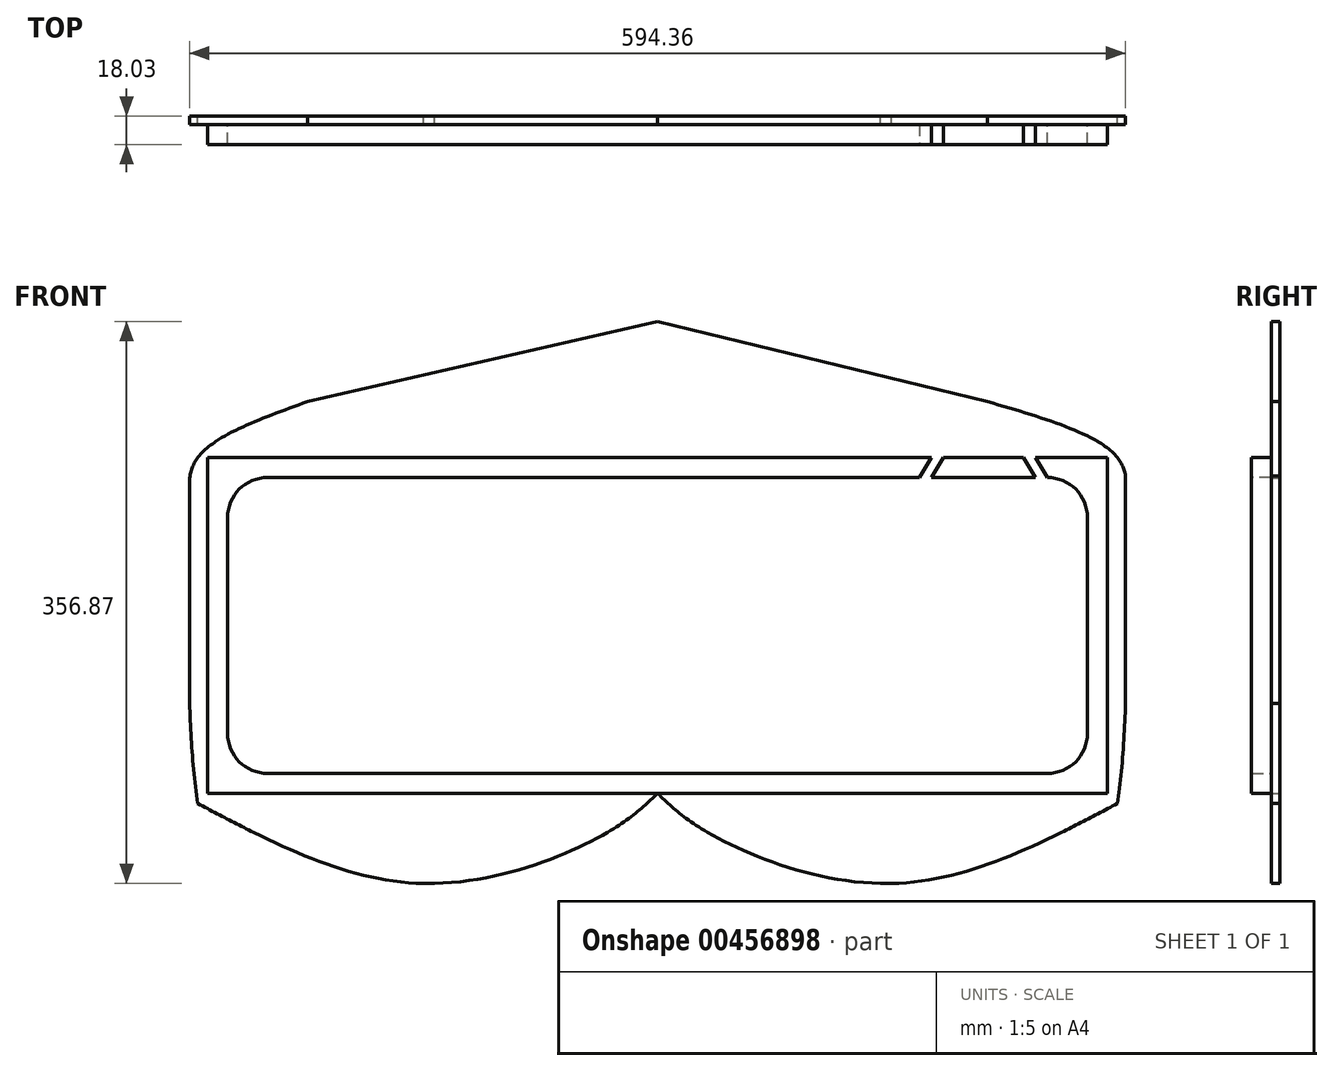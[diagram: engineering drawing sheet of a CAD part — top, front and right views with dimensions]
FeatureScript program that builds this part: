
annotation { "Feature Type Name" : "Feature", "Feature Type Description" : "" }
export const myFeature = defineFeature(function(context is Context, id is Id, definition is map)
    precondition{}
    {
        {
            var Q0;
            Q0=qCreatedBy(makeId("Front.planeOp"),FACE);
            var sketch = newSketch(context, id + "F0", { "sketchPlane" : qUnion([Q0])});
            skLineSegment(sketch, "E0.bottom", {"start": v(0, 0) * mm, "end": v(-584.2, 0) * mm});
            skLineSegment(sketch, "E0.top", {"start": v(0, 219.7) * mm, "end": v(-584.2, 219.7) * mm});
            skLineSegment(sketch, "E0.left", {"start": v(0, 0) * mm, "end": v(0, 219.7) * mm});
            skLineSegment(sketch, "E0.right", {"start": v(-584.2, 0) * mm, "end": v(-584.2, 219.7) * mm});
            skPoint(sketch, "E1", {"position": v(-292.1, 219.7) * mm});
            skSolve(sketch);
        }
        {
            var Q0;
            Q0=makeQuery(id+"F0.imprint","IMPRINT",FACE,{"disambiguationData":[TD([[makeQuery(id+"F0.imprint","IMPRINT",EDGE,{"derivedFrom":sQuery(id+"F0.wireOp",EDGE,"E0.bottom")}),-1.0]])]});
            extrude(context, id + "F1", {"entities" : qUnion([Q0]), "depth" : 5.33 * mm});
        }
        {
            var Q0;
            Q0=makeQuery(id+"F1.opExtrude","CAP_FACE",FACE,{"disambiguationData":[OSD([sQuery(id+"F0.wireOp",EDGE,"E0.bottom"),sQuery(id+"F0.wireOp",EDGE,"E0.top"),sQuery(id+"F0.wireOp",EDGE,"E0.left"),sQuery(id+"F0.wireOp",EDGE,"E0.right")])],"isStart":false});
            var sketch = newSketch(context, id + "F2", { "sketchPlane" : qUnion([Q0])});
            skLineSegment(sketch, "E2", {"start": v(-577.85, 219.7) * mm, "end": v(-577.85, 6.35) * mm});
            skLineSegment(sketch, "E3", {"start": v(-577.85, 6.35) * mm, "end": v(-6.35, 6.35) * mm});
            skLineSegment(sketch, "E4", {"start": v(-6.35, 6.35) * mm, "end": v(-6.35, 219.71) * mm});
            skLineSegment(sketch, "E5", {"start": v(-6.35, 219.71) * mm, "end": v(-577.85, 219.7) * mm});
            skLineSegment(sketch, "E6", {"start": v(-565.15, 207) * mm, "end": v(-565.15, 19.05) * mm});
            skLineSegment(sketch, "E7", {"start": v(-565.15, 19.05) * mm, "end": v(-19.05, 19.05) * mm});
            skLineSegment(sketch, "E8", {"start": v(-19.05, 19.05) * mm, "end": v(-19.05, 207.01) * mm});
            skLineSegment(sketch, "E9", {"start": v(-19.05, 207.01) * mm, "end": v(-565.15, 207) * mm});
            skSolve(sketch);
        }
        {
            var Q0;
            Q0=makeQuery(id+"F2.imprint","IMPRINT",FACE,{"disambiguationData":[TD([[makeQuery(id+"F2.imprint","IMPRINT",EDGE,{"derivedFrom":sQuery(id+"F2.wireOp",EDGE,"E2")}),1.0]])]});
            extrude(context, id + "F3", {"entities" : qUnion([Q0]), "operationType" : NewBodyOperationType.ADD, "depth" : 12.7 * mm});
        }
        {
            var Q0;
            Q0=makeQuery(id+"F3.opExtrude","SWEPT_EDGE",EDGE,{"disambiguationData":[OSD([sQuery(id+"F2.wireOp",EDGE,"E6"),sQuery(id+"F2.wireOp",EDGE,"E9")])]});
            var Q1;
            Q1=makeQuery(id+"F3.opExtrude","SWEPT_EDGE",EDGE,{"disambiguationData":[OSD([sQuery(id+"F2.wireOp",EDGE,"E8"),sQuery(id+"F2.wireOp",EDGE,"E9")])]});
            var Q2;
            Q2=makeQuery(id+"F3.opExtrude","SWEPT_EDGE",EDGE,{"disambiguationData":[OSD([sQuery(id+"F2.wireOp",EDGE,"E7"),sQuery(id+"F2.wireOp",EDGE,"E8")])]});
            var Q3;
            Q3=makeQuery(id+"F3.opExtrude","SWEPT_EDGE",EDGE,{"disambiguationData":[OSD([sQuery(id+"F2.wireOp",EDGE,"E6"),sQuery(id+"F2.wireOp",EDGE,"E7")])]});
            fillet(context, id + "F4", {"entities" : qUnion([Q0, Q1, Q2, Q3]), "radius" : 25.4 * mm, "tangentPropagation" : true, "allowEdgeOverflow" : false});
        }
        {
            var Q0;
            Q0=makeQuery(id+"F3.opExtrude","CAP_FACE",FACE,{"disambiguationData":[OSD([sQuery(id+"F2.wireOp",EDGE,"E2"),sQuery(id+"F2.wireOp",EDGE,"E3"),sQuery(id+"F2.wireOp",EDGE,"E4"),sQuery(id+"F2.wireOp",EDGE,"E5"),sQuery(id+"F2.wireOp",EDGE,"E6"),sQuery(id+"F2.wireOp",EDGE,"E7"),sQuery(id+"F2.wireOp",EDGE,"E8"),sQuery(id+"F2.wireOp",EDGE,"E9")])],"isStart":false});
            var sketch = newSketch(context, id + "F5", { "sketchPlane" : qUnion([Q0])});
            skPoint(sketch, "E10", {"position": v(-118.11, 219.7) * mm});
            skPoint(sketch, "E11", {"position": v(-110.5, 219.7) * mm});
            skPoint(sketch, "E12", {"position": v(-59.69, 219.7) * mm});
            skPoint(sketch, "E13", {"position": v(-52.07, 219.7) * mm});
            skPoint(sketch, "E14", {"position": v(-376.28, 272.75) * mm});
            skPoint(sketch, "E15", {"position": v(-12.7, 0) * mm});
            skPoint(sketch, "E16", {"position": v(-20.32, 0) * mm});
            skLineSegment(sketch, "E17", {"start": v(-20.32, 0) * mm, "end": v(-12.7, 0) * mm});
            skPoint(sketch, "E18", {"position": v(-118.11, 207.01) * mm});
            skPoint(sketch, "E19", {"position": v(-125.73, 207.01) * mm});
            skLineSegment(sketch, "E20", {"start": v(-125.73, 207.01) * mm, "end": v(-118.11, 219.7) * mm});
            skLineSegment(sketch, "E21", {"start": v(-125.73, 207.01) * mm, "end": v(-118.11, 207.01) * mm});
            skLineSegment(sketch, "E22", {"start": v(-118.11, 207.01) * mm, "end": v(-110.5, 219.7) * mm});
            skLineSegment(sketch, "E23", {"start": v(-118.11, 219.7) * mm, "end": v(-110.5, 219.7) * mm});
            skLineSegment(sketch, "E24", {"start": v(-59.69, 219.7) * mm, "end": v(-52.07, 219.7) * mm});
            skLineSegment(sketch, "E25", {"start": v(-110.5, 219.7) * mm, "end": v(-59.69, 219.7) * mm});
            skLineSegment(sketch, "E26", {"start": v(-59.69, 219.7) * mm, "end": v(-110.5, 219.7) * mm});
            skLineSegment(sketch, "E27", {"start": v(-110.5, 219.7) * mm, "end": v(-113.58, 214.56) * mm});
            skPoint(sketch, "E28", {"position": v(-44.45, 207.01) * mm});
            skPoint(sketch, "E29", {"position": v(-52.07, 207.01) * mm});
            skLineSegment(sketch, "E30", {"start": v(-59.69, 219.7) * mm, "end": v(-52.07, 207.01) * mm});
            skLineSegment(sketch, "E31", {"start": v(-52.07, 219.7) * mm, "end": v(-44.45, 207.01) * mm});
            skLineSegment(sketch, "E32", {"start": v(-52.07, 207.01) * mm, "end": v(-44.45, 207.01) * mm});
            skLineSegment(sketch, "E33", {"start": v(-52.07, 219.7) * mm, "end": v(-59.69, 219.7) * mm});
            skPoint(sketch, "E34", {"position": v(-56.6, 214.56) * mm});
            skLineSegment(sketch, "E35", {"start": v(-113.58, 214.56) * mm, "end": v(-56.6, 214.56) * mm});
            skSolve(sketch);
        }
        {
            var Q0;
            Q0=makeQuery(id+"F5.imprint","IMPRINT",FACE,{"disambiguationData":[TD([[makeQuery(id+"F5.imprint","IMPRINT",EDGE,{"derivedFrom":sQuery(id+"F5.wireOp",EDGE,"E20")}),-1.0]])]});
            var Q1;
            {var subQ8=sQuery(id+"F5.wireOp",EDGE,"RZINdJYM-ykuw-GilU-JIjt-DnibDYUsXZuo");Q1=makeQuery(id+"F5.imprint","IMPRINT",FACE,{"disambiguationData":[TD([[makeQuery(id+"F5.imprint","IMPRINT",EDGE,{"derivedFrom":subQ8}),1.0]])]});}
            var Q2;
            Q2=makeQuery(id+"F5.imprint","IMPRINT",FACE,{"disambiguationData":[TD([[makeQuery(id+"F5.imprint","IMPRINT",EDGE,{"derivedFrom":sQuery(id+"F5.wireOp",EDGE,"RZINdJYM-ykuw-GilU-JIjt-DnibDYUsXZuo")}),-1.0]])]});
            var Q3;
            Q3=makeQuery(id+"F5.imprint","IMPRINT",FACE,{"disambiguationData":[TD([[makeQuery(id+"F5.imprint","IMPRINT",EDGE,{"derivedFrom":sQuery(id+"F5.wireOp",EDGE,"NQJIxGkc-Vixr-o2zM-VUe3-bVQ5EoZFKsab")}),1.0]])]});
            var Q4;
            Q4=makeQuery(id+"F5.imprint","IMPRINT",FACE,{"disambiguationData":[TD([[makeQuery(id+"F5.imprint","IMPRINT",EDGE,{"derivedFrom":sQuery(id+"F5.wireOp",EDGE,"E30")}),1.0]])]});
            var Q5;
            {var subQ0=sQuery(id+"F5.wireOp",EDGE,"E26");Q5=makeQuery(id+"F5.imprint","IMPRINT",FACE,{"disambiguationData":[TD([[makeQuery(id+"F5.imprint","IMPRINT",EDGE,{"derivedFrom":subQ0}),1.0]])]});}
            extrude(context, id + "F6", {"entities" : qUnion([Q0, Q1, Q2, Q3, Q4, Q5]), "operationType" : NewBodyOperationType.REMOVE, "oppositeDirection" : true, "depth" : 12.7 * mm});
        }
        {
            var Q0;
            Q0=makeQuery(id+"F1.opExtrude","CAP_FACE",FACE,{"disambiguationData":[OSD([sQuery(id+"F0.wireOp",EDGE,"E0.bottom"),sQuery(id+"F0.wireOp",EDGE,"E0.top"),sQuery(id+"F0.wireOp",EDGE,"E0.left"),sQuery(id+"F0.wireOp",EDGE,"E0.right")])],"isStart":true});
            var sketch = newSketch(context, id + "F7", { "sketchPlane" : qUnion([Q0])});
            skLineSegment(sketch, "E36", {"start": v(0, 0) * mm, "end": v(-5.08, 0) * mm});
            skLineSegment(sketch, "E37", {"start": v(-5.08, 0) * mm, "end": v(-5.08, 229.87) * mm});
            skLineSegment(sketch, "E38", {"start": v(-5.08, 229.87) * mm, "end": v(589.28, 229.87) * mm});
            skLineSegment(sketch, "E39", {"start": v(589.28, 229.87) * mm, "end": v(589.28, 0) * mm});
            skLineSegment(sketch, "E40", {"start": v(589.28, 0) * mm, "end": v(584.2, 0) * mm});
            skPoint(sketch, "E41", {"position": v(589.28, 114.93) * mm});
            skPoint(sketch, "E42", {"position": v(584.2, 109.85) * mm});
            skPoint(sketch, "E43", {"position": v(292.1, 229.87) * mm});
            skPoint(sketch, "E44", {"position": v(292.1, 219.7) * mm});
            skPoint(sketch, "E45", {"position": v(-5.08, 114.93) * mm});
            skPoint(sketch, "E46", {"position": v(0, 109.85) * mm});
            skPoint(sketch, "E47", {"position": v(538.48, 229.87) * mm});
            skPoint(sketch, "E48", {"position": v(45.72, 229.87) * mm});
            skPoint(sketch, "E49", {"position": v(-5.08, 191.77) * mm});
            skPoint(sketch, "E50", {"position": v(589.28, 191.77) * mm});
            skPoint(sketch, "E51", {"position": v(584.2, 183.25) * mm});
            skPoint(sketch, "E52", {"position": v(0, 176.13) * mm});
            skPoint(sketch, "E53", {"position": v(589.28, 63.5) * mm});
            skPoint(sketch, "E54", {"position": v(-5.08, 63.5) * mm});
            skPoint(sketch, "E55", {"position": v(0, 219.7) * mm});
            skPoint(sketch, "E56", {"position": v(584.2, 219.7) * mm});
            skPoint(sketch, "E57", {"position": v(393.7, 219.7) * mm});
            skPoint(sketch, "E58", {"position": v(190.5, 219.7) * mm});
            skLineSegment(sketch, "E59", {"start": v(292.1, 219.7) * mm, "end": v(-5.08, 229.87) * mm});
            skLineSegment(sketch, "E60", {"start": v(292.1, 219.7) * mm, "end": v(589.28, 229.87) * mm});
            skLineSegment(sketch, "E61", {"start": v(589.28, -18.42) * mm, "end": v(-5.08, -18.42) * mm});
            skLineSegment(sketch, "E62", {"start": v(589.28, 0) * mm, "end": v(589.28, -18.42) * mm});
            skLineSegment(sketch, "E63", {"start": v(292.1, 229.87) * mm, "end": v(292.1, 306.07) * mm});
            skPoint(sketch, "E64", {"position": v(292.1, -18.42) * mm});
            skLineSegment(sketch, "E65", {"start": v(589.28, -18.42) * mm, "end": v(589.28, -50.8) * mm});
            skLineSegment(sketch, "E66", {"start": v(589.28, -50.8) * mm, "end": v(292.1, -50.8) * mm});
            skPoint(sketch, "E67", {"position": v(292.1, 0) * mm});
            skPoint(sketch, "E68", {"position": v(440.69, -50.8) * mm});
            skLineSegment(sketch, "E69", {"start": v(292.1, -50.8) * mm, "end": v(-4.91, -50.8) * mm});
            skLineSegment(sketch, "E70", {"start": v(-4.91, -50.8) * mm, "end": v(-5.08, -18.42) * mm});
            skPoint(sketch, "E71", {"position": v(143.6, -50.8) * mm});
            skPoint(sketch, "E72", {"position": v(551.18, -18.42) * mm});
            skPoint(sketch, "E73", {"position": v(33.02, -18.42) * mm});
            skPoint(sketch, "E74", {"position": v(6.35, 219.7) * mm});
            skPoint(sketch, "E75", {"position": v(577.85, 219.7) * mm});
            skPoint(sketch, "E76", {"position": v(6.35, 0) * mm});
            skPoint(sketch, "E77", {"position": v(577.85, 0) * mm});
            skPoint(sketch, "E78", {"position": v(82.55, 229.87) * mm});
            skPoint(sketch, "E79", {"position": v(514.35, 229.87) * mm});
            skLineSegment(sketch, "E80", {"start": v(82.55, 229.87) * mm, "end": v(82.55, 255.27) * mm});
            skLineSegment(sketch, "E81", {"start": v(514.35, 229.87) * mm, "end": v(514.35, 255.27) * mm});
            skLineSegment(sketch, "E82", {"start": v(292.1, 0) * mm, "end": v(292.1, 6.35) * mm});
            skPoint(sketch, "E83", {"position": v(323.85, -18.42) * mm});
            skPoint(sketch, "E84", {"position": v(260.35, -18.42) * mm});
            skFitSpline(sketch, "E85", {"points": [v(292.1, 6.35) * mm, v(323.85, -18.42) * mm, v(440.69, -50.8) * mm, v(584.2, 0) * mm], "startDerivative": vector(117.09, -111.78) * mm, "endDerivative": vector(338.96, 179.53) * mm});
            skFitSpline(sketch, "E86", {"points": [v(292.1, 6.35) * mm, v(260.35, -18.42) * mm, v(143.6, -50.8) * mm, v(0, 0) * mm], "startDerivative": vector(-117.11, -111.77) * mm, "endDerivative": vector(-339.14, 179.5) * mm});
            skFitSpline(sketch, "E87", {"points": [v(514.35, 255.27) * mm, v(292.1, 306.07) * mm], "startDerivative": vector(-222.25, 50.8) * mm, "endDerivative": vector(-222.25, 50.8) * mm});
            skFitSpline(sketch, "E88", {"points": [v(514.35, 255.27) * mm, v(584.2, 219.7) * mm, v(589.28, 191.77) * mm], "startDerivative": vector(142.6, -51.54) * mm, "endDerivative": vector(-4.96, -77.63) * mm});
            skFitSpline(sketch, "E89", {"points": [v(584.2, 0) * mm, v(589.28, 63.5) * mm, v(589.28, 114.93) * mm], "startDerivative": vector(16.08, 110.78) * mm, "endDerivative": vector(0, 114.64) * mm});
            skFitSpline(sketch, "E90", {"points": [v(0, 0) * mm, v(-5.08, 63.5) * mm, v(-5.08, 114.94) * mm], "startDerivative": vector(-15.41, 98.4) * mm, "endDerivative": vector(0, 110.04) * mm});
            skFitSpline(sketch, "E91", {"points": [v(292.1, 306.07) * mm, v(82.55, 255.27) * mm], "startDerivative": vector(-209.55, -50.8) * mm, "endDerivative": vector(-209.55, -50.8) * mm});
            skFitSpline(sketch, "E92", {"points": [v(82.55, 255.27) * mm, v(0, 219.7) * mm, v(-5.08, 191.77) * mm], "startDerivative": vector(-165.7, -48.47) * mm, "endDerivative": vector(6.54, -81.62) * mm});
            skSolve(sketch);
        }
        {
            var Q0;
            {var subQ0=sQuery(id+"F7.wireOp",EDGE,"E82");Q0=makeQuery(id+"F7.imprint","IMPRINT",FACE,{"disambiguationData":[TD([[makeQuery(id+"F7.imprint","IMPRINT",EDGE,{"derivedFrom":subQ0}),1.0]])]});}
            var Q1;
            {var subQ0=sQuery(id+"F7.wireOp",EDGE,"E82");Q1=makeQuery(id+"F7.imprint","IMPRINT",FACE,{"disambiguationData":[TD([[makeQuery(id+"F7.imprint","IMPRINT",EDGE,{"derivedFrom":subQ0}),-1.0]])]});}
            extrude(context, id + "F8", {"entities" : qUnion([Q0, Q1]), "operationType" : NewBodyOperationType.REMOVE, "depth" : -5.33 * mm});
        }
        {
            var Q0;
            {var subQ0=sQuery(id+"F7.wireOp",EDGE,"E80");Q0=makeQuery(id+"F7.imprint","IMPRINT",FACE,{"disambiguationData":[TD([[makeQuery(id+"F7.imprint","IMPRINT",EDGE,{"derivedFrom":subQ0}),1.0]])]});}
            var Q1;
            {var subQ0=sQuery(id+"F7.wireOp",EDGE,"E63");Q1=makeQuery(id+"F7.imprint","IMPRINT",FACE,{"disambiguationData":[TD([[makeQuery(id+"F7.imprint","IMPRINT",EDGE,{"derivedFrom":subQ0}),1.0]])]});}
            var Q2;
            {var subQ0=sQuery(id+"F7.wireOp",EDGE,"E63");Q2=makeQuery(id+"F7.imprint","IMPRINT",FACE,{"disambiguationData":[TD([[makeQuery(id+"F7.imprint","IMPRINT",EDGE,{"derivedFrom":subQ0}),-1.0]])]});}
            var Q3;
            {var subQ0=sQuery(id+"F7.wireOp",EDGE,"E81");Q3=makeQuery(id+"F7.imprint","IMPRINT",FACE,{"disambiguationData":[TD([[makeQuery(id+"F7.imprint","IMPRINT",EDGE,{"derivedFrom":subQ0}),-1.0]])]});}
            var Q4;
            {var subQ0=sQuery(id+"F7.wireOp",EDGE,"E60");var subQ3=sQuery(id+"F7.wireOp",EDGE,"c924a81b-7c33-454b-bec7-e8dcdf9a45a6");var subQ4=makeQuery(id+"F7.imprint","INTERSECT",VERTEX,{"derivedFrom":[subQ0,subQ3]});Q4=makeQuery(id+"F7.imprint","IMPRINT",FACE,{"disambiguationData":[TD([[makeQuery(id+"F7.imprint","IMPRINT",EDGE,{"disambiguationData":[TD([[subQ4,1.0]])],"derivedFrom":subQ0}),-1.0]])]});}
            var Q5;
            {var subQ0=sQuery(id+"F7.wireOp",EDGE,"E38");var subQ7=makeQuery(id+"F7.imprint","INTERSECT",VERTEX,{"derivedFrom":[subQ0,sQuery(id+"F7.wireOp",EDGE,"E80")]});Q5=makeQuery(id+"F7.imprint","IMPRINT",FACE,{"disambiguationData":[TD([[makeQuery(id+"F7.imprint","IMPRINT",EDGE,{"disambiguationData":[TD([[subQ7,1.0]])],"derivedFrom":subQ0}),-1.0]])]});}
            var Q6;
            {var subQ0=sQuery(id+"F7.wireOp",EDGE,"E59");var subQ3=sQuery(id+"F7.wireOp",EDGE,"3c0d3bf1-8729-4a13-bacb-ae9455c1fce2");var subQ4=makeQuery(id+"F7.imprint","INTERSECT",VERTEX,{"derivedFrom":[subQ0,subQ3]});Q6=makeQuery(id+"F7.imprint","IMPRINT",FACE,{"disambiguationData":[TD([[makeQuery(id+"F7.imprint","IMPRINT",EDGE,{"disambiguationData":[TD([[subQ4,1.0]])],"derivedFrom":subQ0}),1.0]])]});}
            var Q7;
            {var subQ0=sQuery(id+"F7.wireOp",EDGE,"c8baf287-04a5-4912-9b82-47411f5b9158");var subQ1=sQuery(id+"F7.wireOp",EDGE,"E61");var subQ2=makeQuery(id+"F7.imprint","INTERSECT",VERTEX,{"disambiguationData":[OD(0.0)],"derivedFrom":[subQ1,subQ0]});Q7=makeQuery(id+"F7.imprint","IMPRINT",FACE,{"disambiguationData":[TD([[makeQuery(id+"F7.imprint","IMPRINT",EDGE,{"disambiguationData":[TD([[subQ2,1.0]])],"derivedFrom":subQ1}),-1.0]])]});}
            var Q8;
            {var subQ0=sQuery(id+"F7.wireOp",EDGE,"c8baf287-04a5-4912-9b82-47411f5b9158");var subQ1=sQuery(id+"F7.wireOp",EDGE,"E61");var subQ2=makeQuery(id+"F7.imprint","INTERSECT",VERTEX,{"disambiguationData":[OD(0.0)],"derivedFrom":[subQ1,subQ0]});Q8=makeQuery(id+"F7.imprint","IMPRINT",FACE,{"disambiguationData":[TD([[makeQuery(id+"F7.imprint","IMPRINT",EDGE,{"disambiguationData":[TD([[subQ2,1.0]])],"derivedFrom":subQ1}),1.0]])]});}
            var Q9;
            {var subQ0=sQuery(id+"F7.wireOp",EDGE,"c47f91c2-344f-4819-b83d-0fa72e82eadb");var subQ1=sQuery(id+"F7.wireOp",EDGE,"E61");var subQ2=makeQuery(id+"F7.imprint","INTERSECT",VERTEX,{"disambiguationData":[OD(0.0)],"derivedFrom":[subQ1,subQ0]});Q9=makeQuery(id+"F7.imprint","IMPRINT",FACE,{"disambiguationData":[TD([[makeQuery(id+"F7.imprint","IMPRINT",EDGE,{"disambiguationData":[TD([[subQ2,-1.0]])],"derivedFrom":subQ1}),-1.0]])]});}
            var Q10;
            {var subQ0=sQuery(id+"F7.wireOp",EDGE,"c47f91c2-344f-4819-b83d-0fa72e82eadb");var subQ1=sQuery(id+"F7.wireOp",EDGE,"E61");var subQ2=makeQuery(id+"F7.imprint","INTERSECT",VERTEX,{"disambiguationData":[OD(0.0)],"derivedFrom":[subQ1,subQ0]});Q10=makeQuery(id+"F7.imprint","IMPRINT",FACE,{"disambiguationData":[TD([[makeQuery(id+"F7.imprint","IMPRINT",EDGE,{"disambiguationData":[TD([[subQ2,-1.0]])],"derivedFrom":subQ1}),1.0]])]});}
            var Q11;
            {var subQ0=sQuery(id+"F7.wireOp",EDGE,"E85");var subQ1=sQuery(id+"F7.wireOp",EDGE,"E61");var subQ2=makeQuery(id+"F7.imprint","INTERSECT",VERTEX,{"disambiguationData":[OD(0.0)],"derivedFrom":[subQ1,subQ0]});Q11=makeQuery(id+"F7.imprint","IMPRINT",FACE,{"disambiguationData":[TD([[makeQuery(id+"F7.imprint","IMPRINT",EDGE,{"disambiguationData":[TD([[subQ2,-1.0]])],"derivedFrom":subQ1}),1.0]])]});}
            var Q12;
            {var subQ0=sQuery(id+"F7.wireOp",EDGE,"E85");var subQ1=sQuery(id+"F7.wireOp",EDGE,"E61");var subQ2=makeQuery(id+"F7.imprint","INTERSECT",VERTEX,{"disambiguationData":[OD(0.0)],"derivedFrom":[subQ1,subQ0]});Q12=makeQuery(id+"F7.imprint","IMPRINT",FACE,{"disambiguationData":[TD([[makeQuery(id+"F7.imprint","IMPRINT",EDGE,{"disambiguationData":[TD([[subQ2,-1.0]])],"derivedFrom":subQ1}),-1.0]])]});}
            var Q13;
            {var subQ0=sQuery(id+"F7.wireOp",EDGE,"E86");var subQ1=sQuery(id+"F7.wireOp",EDGE,"E61");var subQ2=makeQuery(id+"F7.imprint","INTERSECT",VERTEX,{"disambiguationData":[OD(0.0)],"derivedFrom":[subQ1,subQ0]});Q13=makeQuery(id+"F7.imprint","IMPRINT",FACE,{"disambiguationData":[TD([[makeQuery(id+"F7.imprint","IMPRINT",EDGE,{"disambiguationData":[TD([[subQ2,1.0]])],"derivedFrom":subQ1}),1.0]])]});}
            var Q14;
            {var subQ0=sQuery(id+"F7.wireOp",EDGE,"E86");var subQ1=sQuery(id+"F7.wireOp",EDGE,"E61");var subQ2=makeQuery(id+"F7.imprint","INTERSECT",VERTEX,{"disambiguationData":[OD(0.0)],"derivedFrom":[subQ1,subQ0]});Q14=makeQuery(id+"F7.imprint","IMPRINT",FACE,{"disambiguationData":[TD([[makeQuery(id+"F7.imprint","IMPRINT",EDGE,{"disambiguationData":[TD([[subQ2,1.0]])],"derivedFrom":subQ1}),-1.0]])]});}
            var Q15;
            {var subQ4=makeQuery(id+"F1.opExtrude","CAP_EDGE",EDGE,{"disambiguationData":[OSD([sQuery(id+"F0.wireOp",EDGE,"E0.right")])],"isStart":true});Q15=makeQuery(id+"F7.imprint","IMPRINT",FACE,{"disambiguationData":[TD([[makeQuery(id+"F7.imprint","IMPRINT",EDGE,{"derivedFrom":subQ4}),-1.0]])]});}
            var Q16;
            {var subQ4=makeQuery(id+"F1.opExtrude","CAP_EDGE",EDGE,{"disambiguationData":[OSD([sQuery(id+"F0.wireOp",EDGE,"E0.left")])],"isStart":true});Q16=makeQuery(id+"F7.imprint","IMPRINT",FACE,{"disambiguationData":[TD([[makeQuery(id+"F7.imprint","IMPRINT",EDGE,{"derivedFrom":subQ4}),1.0]])]});}
            extrude(context, id + "F9", {"entities" : qUnion([Q0, Q1, Q2, Q3, Q4, Q5, Q6, Q7, Q8, Q9, Q10, Q11, Q12, Q13, Q14, Q15, Q16]), "operationType" : NewBodyOperationType.ADD, "depth" : -5.33 * mm});
        }
    });
